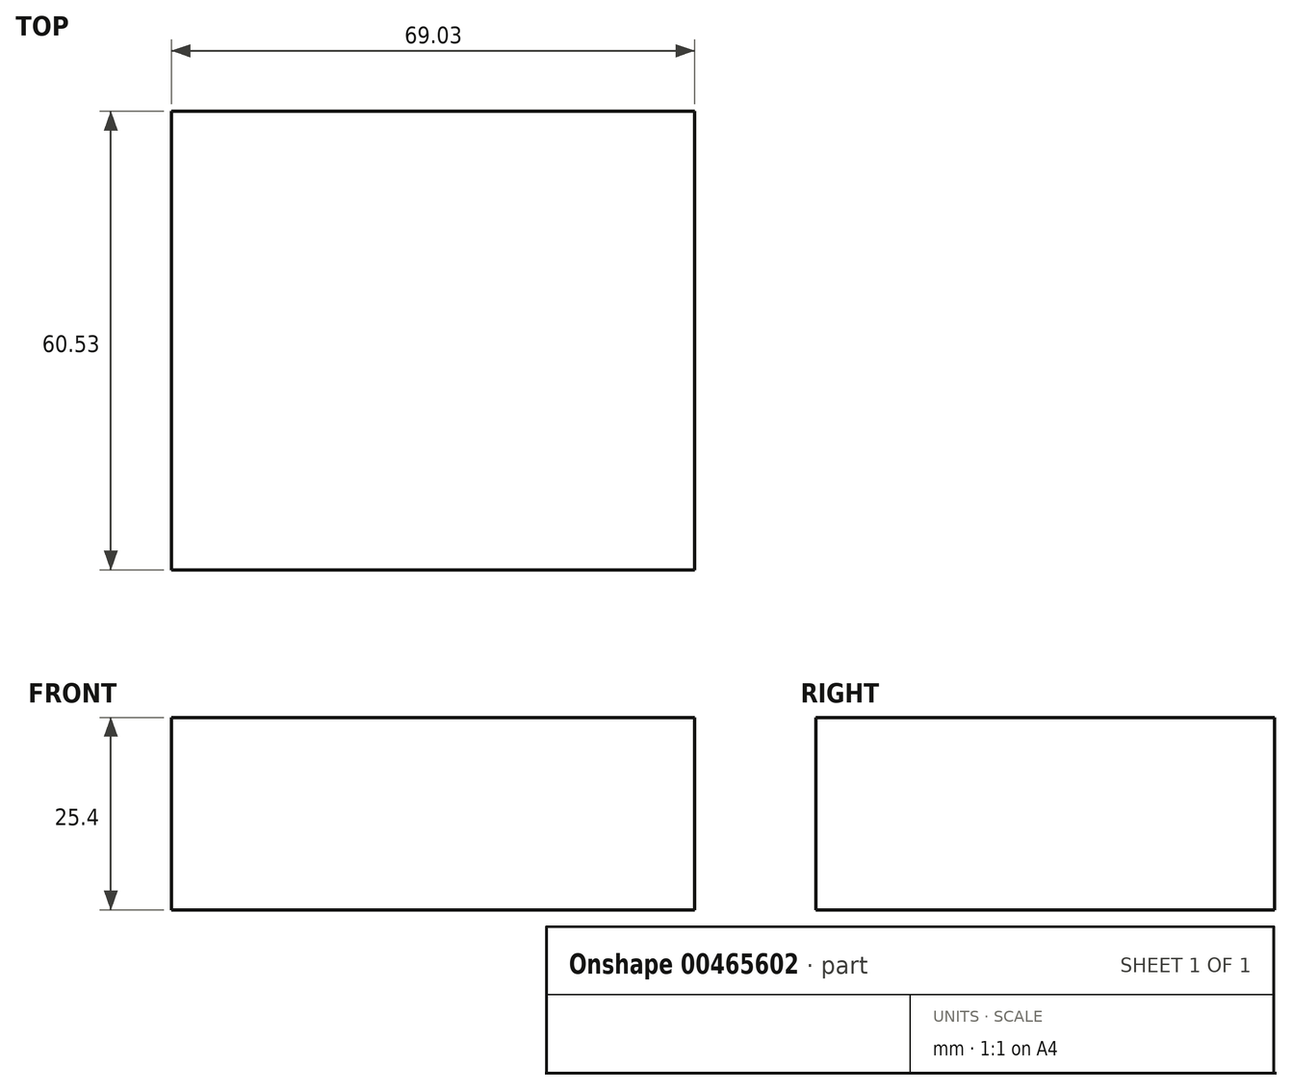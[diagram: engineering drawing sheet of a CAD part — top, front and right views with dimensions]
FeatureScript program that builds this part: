
annotation { "Feature Type Name" : "Feature", "Feature Type Description" : "" }
export const myFeature = defineFeature(function(context is Context, id is Id, definition is map)
    precondition{}
    {
        {
            var Q0;
            Q0=qCreatedBy(makeId("Top.planeOp"),FACE);
            var sketch = newSketch(context, id + "F0", { "sketchPlane" : qUnion([Q0])});
            skLineSegment(sketch, "E0.bottom", {"start": v(-0.1, 56.4) * mm, "end": v(68.94, 56.4) * mm});
            skLineSegment(sketch, "E0.top", {"start": v(-0.1, -4.12) * mm, "end": v(68.94, -4.12) * mm});
            skLineSegment(sketch, "E0.left", {"start": v(-0.1, 56.4) * mm, "end": v(-0.1, -4.12) * mm});
            skLineSegment(sketch, "E0.right", {"start": v(68.94, 56.4) * mm, "end": v(68.94, -4.12) * mm});
            skSolve(sketch);
        }
        {
            var Q0;
            Q0=makeQuery(id+"F0.imprint","IMPRINT",FACE,{"disambiguationData":[TD([[makeQuery(id+"F0.imprint","IMPRINT",EDGE,{"derivedFrom":sQuery(id+"F0.wireOp",EDGE,"E0.bottom")}),-1.0]])]});
            extrude(context, id + "F1", {"entities" : qUnion([Q0]), "depth" : 25.4 * mm});
        }
    });
